# Revit family: IEK_Выключатель_ОткрытойУстановки_С Инд 10А двухклавишный IP20_ОКТАВА
name_source: partatom
category: Выключатели
units: mm (PartAtom-declared; Revit-internal decimal feet)

## family parameters
Всегда вертикально = Да
На основе рабочей плоскости = Нет
Общий = Нет
При загрузке вырезать с полостями = Нет
Размер круглого соединителя = Использовать диаметр
Сохранять ориентацию аннотаций = Да
Тип детали = Переключатель
Точка расчета площади = Нет

## types (2) — shared parameters
ADSK_URL страницы изделия = https://www.iek.ru
ADSK_Версия Revit = 2019
ADSK_Версия семейства = 1.0
ADSK_Группирование = III ЭЛЕКТРОУСТАНОВОЧНЫЕ И ЭЛЕКТРОМОНТАЖНЫЕ ИЗДЕЛИЯ
ADSK_Единица измерения = шт
ADSK_Завод-изготовитель = IEK
ADSK_Количество фаз = 1
ADSK_Количество фаз числовое = 1
ADSK_Марка = ОКТАВА
ADSK_Масса = 0.059
ADSK_Материал наименование = Пластик
ADSK_Напряжение = 220 В
IEK_URL = https://www.iek.ru
IEK_Описание = Универсальный дизайн серии открытой установки "ОКТАВА" позволяет устанавливать изделия в квартирах, загородных домах, офисных и производственных помещениях.
KSI_CMa_Строительные материалы = 01.7.14.03
KSI_CPr_Строительные изделия = 20.4.01
Высота = 61 мм
Глубина = 37 мм
Изготовитель = IEK
Степень защиты = IP20
Тип монтажа = Поверхность монтажа (открытая установка)
Ширина = 61 мм

## per-type parameters (varying)
| type | ADSK_Код изделия | ADSK_Материал | ADSK_Наименование | IEK_Цена за единицу |
| ВС20-2-1-ОБ | EVO21-K01-10-DC | Цвет белый | Выключатель 2-клавишный для открытой установки с индикацией ВС20-2-1-ОБ 10А ОКТАВА белый IEK | 127.08 |
| ВС20-2-1-ОД | EVO21-K04-10-DC | Цвет дуб | Выключатель 2-клавишный для открытой установки с индикацией ВС20-2-1-ОД 10А ОКТАВА дуб IEK | 191.46 |
